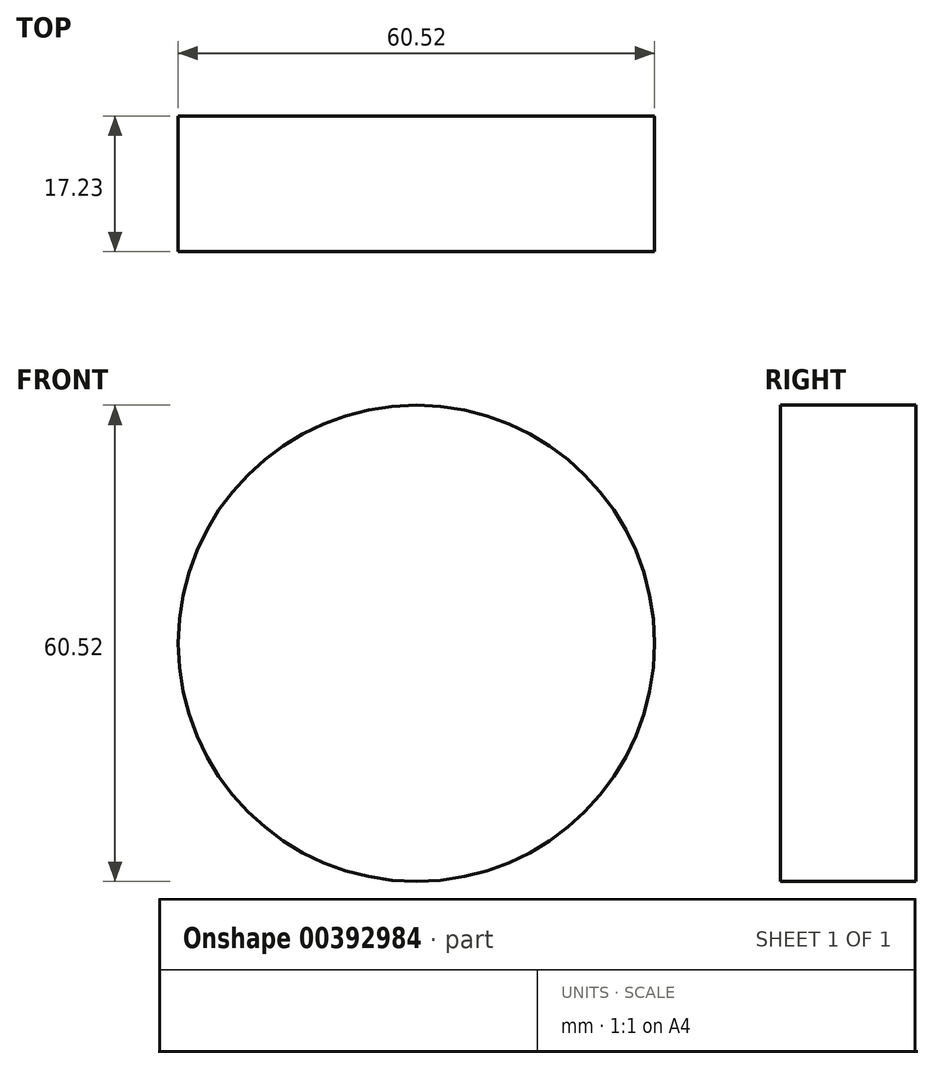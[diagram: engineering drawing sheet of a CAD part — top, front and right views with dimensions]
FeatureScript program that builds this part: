
annotation { "Feature Type Name" : "Feature", "Feature Type Description" : "" }
export const myFeature = defineFeature(function(context is Context, id is Id, definition is map)
    precondition{}
    {
        {
            var Q0;
            Q0=qCreatedBy(makeId("Front.planeOp"),FACE);
            var sketch = newSketch(context, id + "F0", { "sketchPlane" : qUnion([Q0])});
            skCircle(sketch, "E0", {"center": v(0, 0) * mm, "radius": 30.26 * mm});
            skSolve(sketch);
        }
        {
            var Q0;
            Q0=sQuery(id+"F0.wireOp",EDGE,"E0");
            extrude(context, id + "F1", {"bodyType" : ToolBodyType.SURFACE, "surfaceEntities" : qUnion([Q0]), "depth" : 17.23 * mm});
        }
    });
